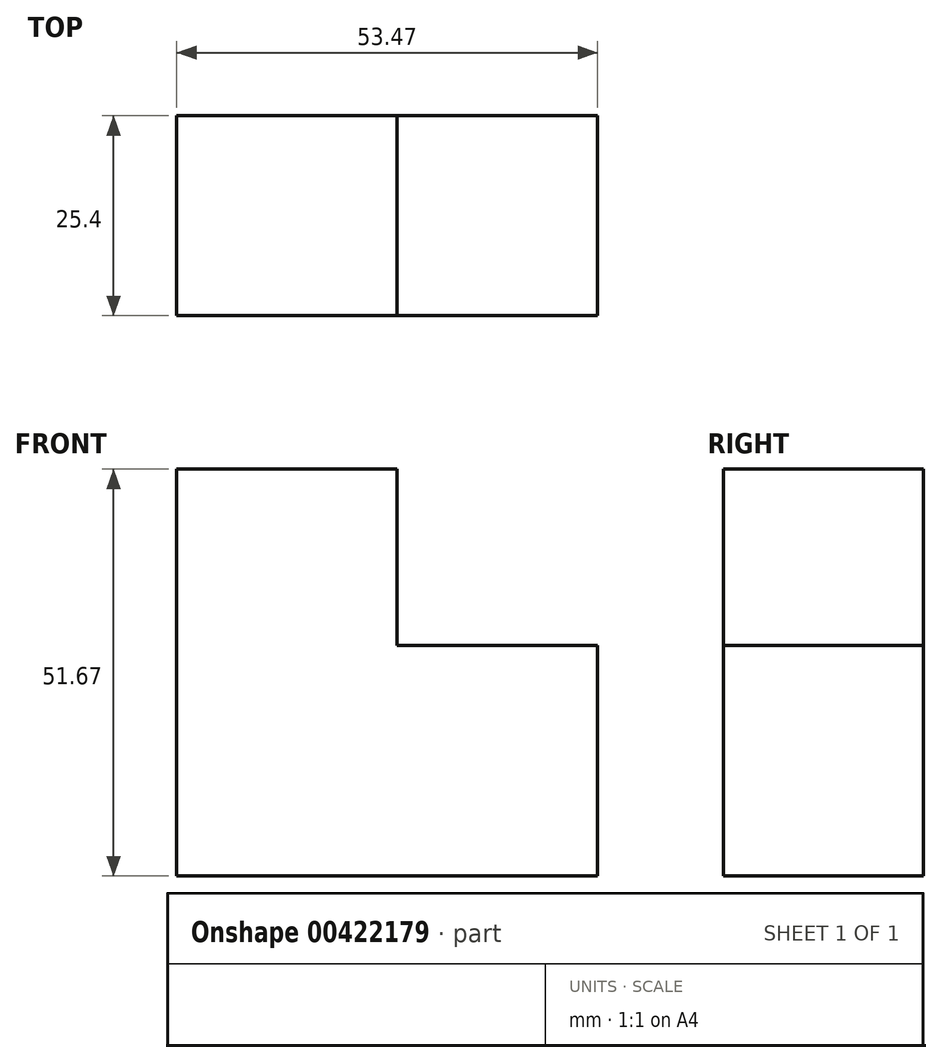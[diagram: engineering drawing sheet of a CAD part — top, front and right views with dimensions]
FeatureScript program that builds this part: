
annotation { "Feature Type Name" : "Feature", "Feature Type Description" : "" }
export const myFeature = defineFeature(function(context is Context, id is Id, definition is map)
    precondition{}
    {
        {
            var Q0;
            Q0=qCreatedBy(makeId("Front.planeOp"),FACE);
            var sketch = newSketch(context, id + "F0", { "sketchPlane" : qUnion([Q0])});
            skLineSegment(sketch, "E0", {"start": v(-65.21, 48.77) * mm, "end": v(-37.2, 48.77) * mm});
            skLineSegment(sketch, "E1", {"start": v(-65.21, 48.77) * mm, "end": v(-65.21, -2.9) * mm});
            skLineSegment(sketch, "E2", {"start": v(-37.2, 48.77) * mm, "end": v(-37.2, 26.38) * mm});
            skLineSegment(sketch, "E3", {"start": v(-37.2, 26.38) * mm, "end": v(-11.74, 26.38) * mm});
            skLineSegment(sketch, "E4", {"start": v(-11.74, 26.38) * mm, "end": v(-11.74, -2.9) * mm});
            skLineSegment(sketch, "E5", {"start": v(-11.74, -2.9) * mm, "end": v(-65.21, -2.9) * mm});
            skSolve(sketch);
        }
        {
            var Q0;
            Q0=makeQuery(id+"F0.imprint","IMPRINT",FACE,{"disambiguationData":[TD([[makeQuery(id+"F0.imprint","IMPRINT",EDGE,{"derivedFrom":sQuery(id+"F0.wireOp",EDGE,"E0")}),-1.0]])]});
            extrude(context, id + "F1", {"entities" : qUnion([Q0]), "depth" : 25.4 * mm});
        }
    });
